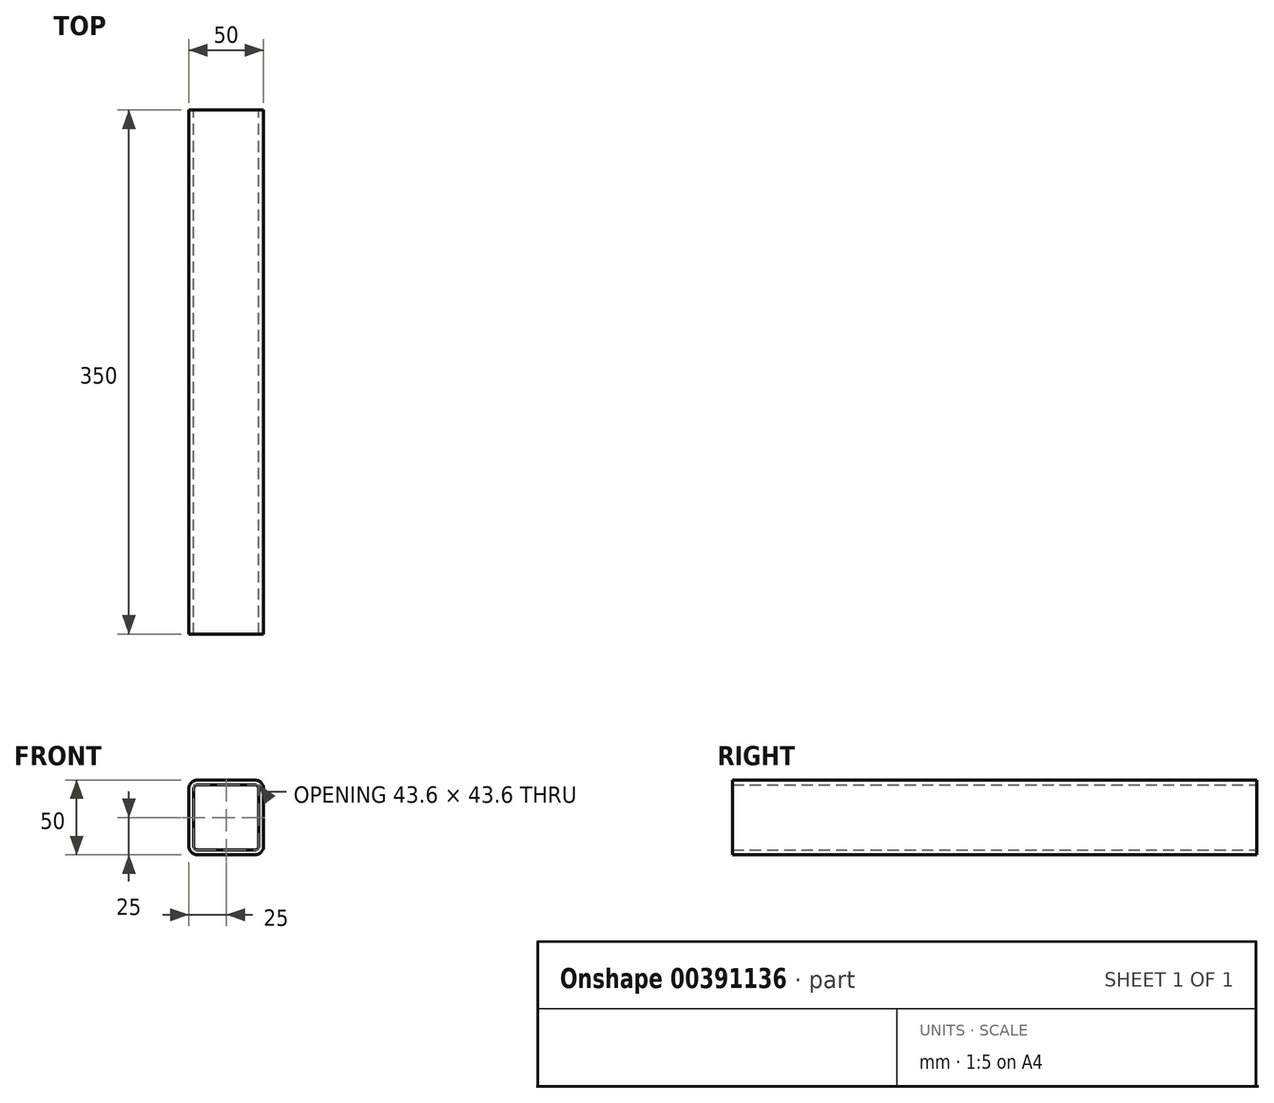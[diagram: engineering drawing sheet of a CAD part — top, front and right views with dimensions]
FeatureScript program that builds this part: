
annotation { "Feature Type Name" : "Feature", "Feature Type Description" : "" }
export const myFeature = defineFeature(function(context is Context, id is Id, definition is map)
    precondition{}
    {
        {
            var Q0;
            Q0=qCreatedBy(makeId("Front.planeOp"),FACE);
            var sketch = newSketch(context, id + "F0", { "sketchPlane" : qUnion([Q0])});
            skLineSegment(sketch, "E0.bottom", {"start": v(-19, 25) * mm, "end": v(19, 25) * mm});
            skLineSegment(sketch, "E0.top", {"start": v(-19, -25) * mm, "end": v(19, -25) * mm});
            skLineSegment(sketch, "E0.left", {"start": v(-25, 19) * mm, "end": v(-25, -19) * mm});
            skLineSegment(sketch, "E0.right", {"start": v(25, 19) * mm, "end": v(25, -19) * mm});
            skPoint(sketch, "E0.middle", {"position": v(0, 0) * mm});
            skPoint(sketch, "E1.visualSharp", {"position": v(25, 25) * mm});
            skArc(sketch, "E1.filletArc", {"start": v(25, 19) * mm, "mid": v(23.24, 23.24) * mm, "end": v(19, 25) * mm});
            skPoint(sketch, "E2.visualSharp", {"position": v(-25, 25) * mm});
            skArc(sketch, "E2.filletArc", {"start": v(-19, 25) * mm, "mid": v(-23.24, 23.24) * mm, "end": v(-25, 19) * mm});
            skPoint(sketch, "E3.visualSharp", {"position": v(-25, -25) * mm});
            skArc(sketch, "E3.filletArc", {"start": v(-25, -19) * mm, "mid": v(-23.24, -23.24) * mm, "end": v(-19, -25) * mm});
            skPoint(sketch, "E4.visualSharp", {"position": v(25, -25) * mm});
            skArc(sketch, "E4.filletArc", {"start": v(19, -25) * mm, "mid": v(23.24, -23.24) * mm, "end": v(25, -19) * mm});
            skArc(sketch, "E5.0", {"start": v(21.8, 19) * mm, "mid": v(20.98, 20.98) * mm, "end": v(19, 21.8) * mm});
            skLineSegment(sketch, "E5.1", {"start": v(-19, 21.8) * mm, "end": v(19, 21.8) * mm});
            skLineSegment(sketch, "E5.2", {"start": v(21.8, 19) * mm, "end": v(21.8, -19) * mm});
            skArc(sketch, "E5.3", {"start": v(-19, 21.8) * mm, "mid": v(-20.98, 20.98) * mm, "end": v(-21.8, 19) * mm});
            skArc(sketch, "E5.4", {"start": v(19, -21.8) * mm, "mid": v(20.98, -20.98) * mm, "end": v(21.8, -19) * mm});
            skLineSegment(sketch, "E5.5", {"start": v(-19, -21.8) * mm, "end": v(19, -21.8) * mm});
            skArc(sketch, "E5.6", {"start": v(-21.8, -19) * mm, "mid": v(-20.98, -20.98) * mm, "end": v(-19, -21.8) * mm});
            skLineSegment(sketch, "E5.7", {"start": v(-21.8, 19) * mm, "end": v(-21.8, -19) * mm});
            skSolve(sketch);
        }
        {
            var Q0;
            Q0=makeQuery(id+"F0.imprint","IMPRINT",FACE,{"disambiguationData":[TD([[makeQuery(id+"F0.imprint","IMPRINT",EDGE,{"derivedFrom":sQuery(id+"F0.wireOp",EDGE,"E0.bottom")}),-1.0]])]});
            extrude(context, id + "F1", {"entities" : qUnion([Q0]), "depth" : 350 * mm});
        }
    });
